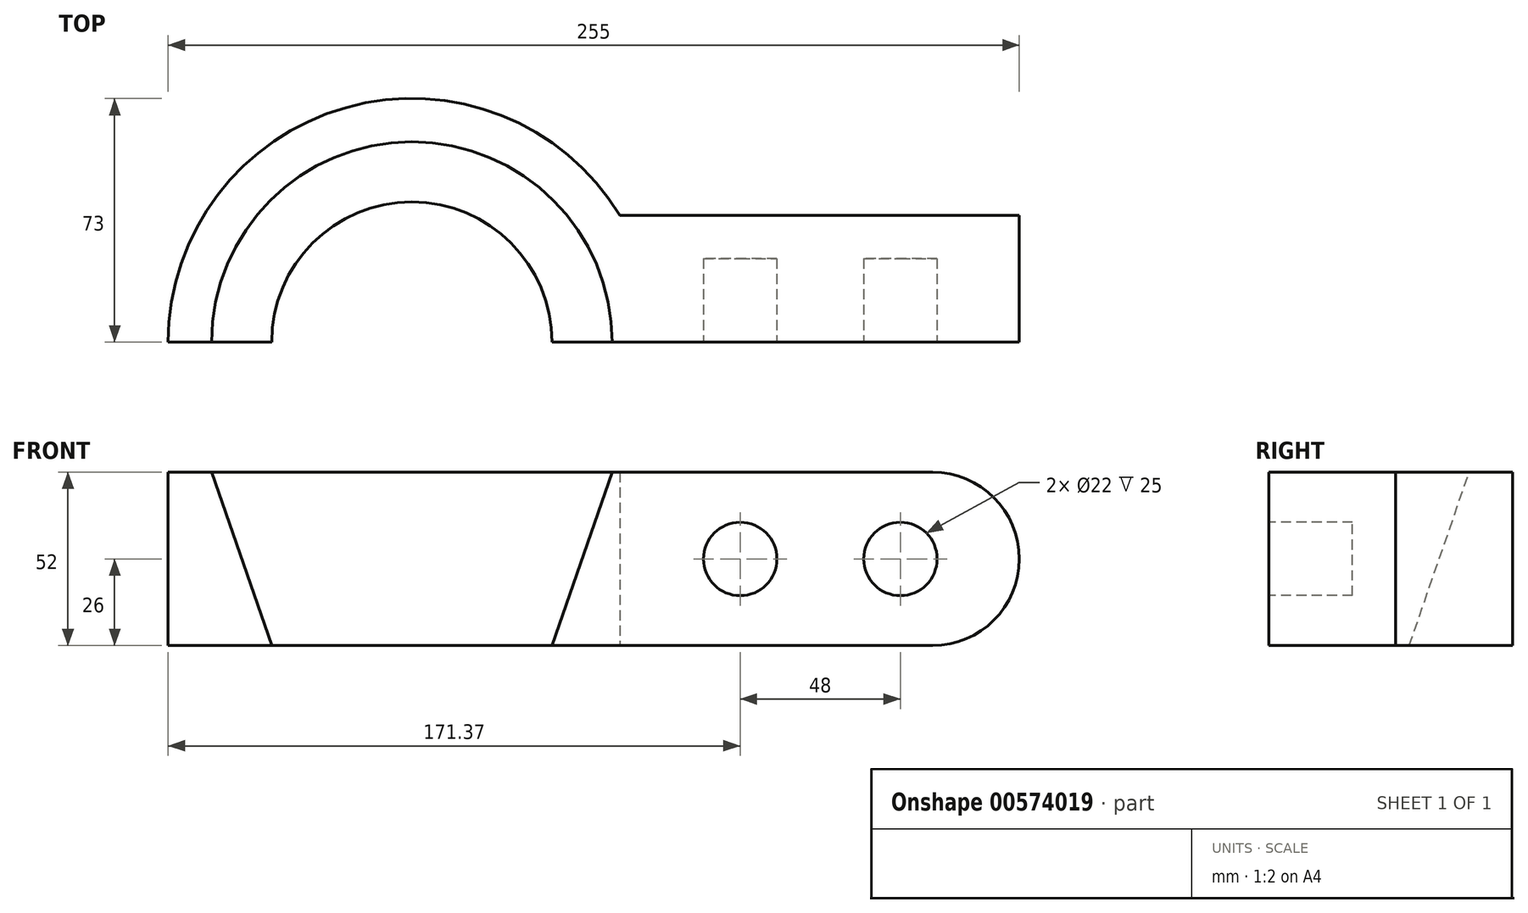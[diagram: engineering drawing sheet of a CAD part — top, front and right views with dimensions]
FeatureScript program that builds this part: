
annotation { "Feature Type Name" : "Feature", "Feature Type Description" : "" }
export const myFeature = defineFeature(function(context is Context, id is Id, definition is map)
    precondition{}
    {
        {
            var Q0;
            Q0=qCreatedBy(makeId("Top.planeOp"),FACE);
            var sketch = newSketch(context, id + "F0", { "sketchPlane" : qUnion([Q0])});
            skArc(sketch, "E0", {"start": v(62.33, 38) * mm, "mid": v(-19.73, 70.28) * mm, "end": v(-73, 0) * mm});
            skLineSegment(sketch, "E1.bottom", {"start": v(0, 0) * mm, "end": v(182, 0) * mm});
            skLineSegment(sketch, "E1.right", {"start": v(182, 0) * mm, "end": v(182, 38) * mm});
            skLineSegment(sketch, "E2", {"start": v(0, 0) * mm, "end": v(-73, 0) * mm});
            skLineSegment(sketch, "E3.trimOffspring", {"start": v(62.33, 38) * mm, "end": v(182, 38) * mm});
            skSolve(sketch);
        }
        {
            var Q0;
            Q0 = qSketchRegion(id + "F0", true);
            extrude(context, id + "F1", {"entities" : qUnion([Q0]), "depth" : 52 * mm, "offsetDistance" : 25 * mm});
        }
        {
            var Q0;
            Q0=makeQuery(id+"F1.opExtrude","SWEPT_FACE",FACE,{"disambiguationData":[OSD([sQuery(id+"F0.wireOp",EDGE,"E1.bottom"),sQuery(id+"F0.wireOp",EDGE,"E2")])]});
            var sketch = newSketch(context, id + "F2", { "sketchPlane" : qUnion([Q0])});
            skLineSegment(sketch, "E4", {"start": v(-60, 52) * mm, "end": v(-42, 0) * mm});
            skLineSegment(sketch, "E5", {"start": v(-42, 0) * mm, "end": v(0, 0) * mm});
            skLineSegment(sketch, "E6", {"start": v(0, 0) * mm, "end": v(0, 52) * mm});
            skLineSegment(sketch, "E7", {"start": v(0, 52) * mm, "end": v(-60, 52) * mm});
            skSolve(sketch);
        }
        {
            var Q0;
            Q0 = qSketchRegion(id + "F2", true);
            var Q1;
            Q1=sQuery(id+"F2.wireOp",EDGE,"E6");
            revolve(context, id + "F3", {"operationType" : NewBodyOperationType.REMOVE, "entities" : qUnion([Q0]), "axis" : qUnion([Q1]), "revolveType" : RevolveType.FULL, "oppositeDirection" : true});
        }
        {
            var Q0;
            {var subQ1=sQuery(id+"F0.wireOp",EDGE,"E2");var subQ2=sQuery(id+"F0.wireOp",EDGE,"E1.right");var subQ3=sQuery(id+"F0.wireOp",EDGE,"E1.bottom");Q0=makeQuery(id+"F3.boolean.opBoolean","SPLIT",FACE,{"disambiguationData":[TD([makeQuery(id+"F1.opExtrude","SWEPT_FACE",FACE,{"disambiguationData":[OSD([subQ2])]})])],"derivedFrom":makeQuery(id+"F1.opExtrude","SWEPT_FACE",FACE,{"disambiguationData":[OSD([subQ3,subQ1])]})});}
            var sketch = newSketch(context, id + "F4", { "sketchPlane" : qUnion([Q0])});
            skCircle(sketch, "E8", {"center": v(98.37, 26) * mm, "radius": 11 * mm});
            skCircle(sketch, "E9", {"center": v(146.37, 26) * mm, "radius": 11 * mm});
            skLineSegment(sketch, "E10", {"start": v(182, 26) * mm, "end": v(-72.9, 26) * mm});
            skPoint(sketch, "E10.endSnap0", {"position": v(182, 26) * mm});
            skSolve(sketch);
        }
        {
            var Q0;
            Q0 = qSketchRegion(id + "F4", true);
            extrude(context, id + "F5", {"entities" : qUnion([Q0]), "operationType" : NewBodyOperationType.REMOVE, "oppositeDirection" : true, "depth" : 25 * mm, "offsetDistance" : 25 * mm});
        }
        {
            var Q0;
            Q0=makeQuery(id+"F1.opExtrude","CAP_EDGE",EDGE,{"disambiguationData":[OSD([sQuery(id+"F0.wireOp",EDGE,"E1.right")])],"isStart":false});
            fillet(context, id + "F6", {"entities" : qUnion([Q0]), "radius" : 26 * mm, "tangentPropagation" : true, "allowEdgeOverflow" : false});
        }
        {
            var Q0;
            Q0=makeQuery(id+"F1.opExtrude","CAP_EDGE",EDGE,{"disambiguationData":[OSD([sQuery(id+"F0.wireOp",EDGE,"E1.right")])],"isStart":true});
            fillet(context, id + "F7", {"entities" : qUnion([Q0]), "radius" : 26 * mm, "tangentPropagation" : true, "allowEdgeOverflow" : false});
        }
    });
